# Revit family: TCF34570GAC_TAC
name_source: partatom
category: 衛生器具
revit_build: Autodesk Revit 2018 (Build: 20170223_1515(x64)
units: mm (PartAtom-declared; Revit-internal decimal feet)

## family parameters
OmniClass タイトル = Sanitary, Laundry, and Cleaning Equipment
OmniClass 番号 = 23.45.00.00
パーツ タイプ = 標準
ロード時にボイドで切り取り = いいえ
丸型コネクタ寸法 = 直径を使用
作業面ベース = いいえ
共有 = いいえ
常に垂直 = はい
部屋計算ポイント = いいえ

## types (1)
- TCF34570GAC_TAC
    Cold Water Inlet = はい
    Finish = White
    Height = 130  [stored 0.426509 ft]
    Length = 540  [stored 1.77165 ft]
    Material = Plastic
    URL = https://www.toto.com
    Voltage = 220V-240V
    Width = 383  [stored 1.25656 ft]
    モデル = TCF34570GAA/TCF34320GAA
    排気配管 = いいえ
    排水配管 = いいえ
    水配管 = はい
    温水配管 = いいえ
    製造元 = TOTO LTD.
    説明 = Spray Seat WASHLET S5

note: [stored X ft] marks values corroborated as IEEE doubles in the binary element streams (Revit-internal decimal feet)

## geometry (parser evidence)
native form markers: Sweep x2
no freeform markers — native parametric forms only
